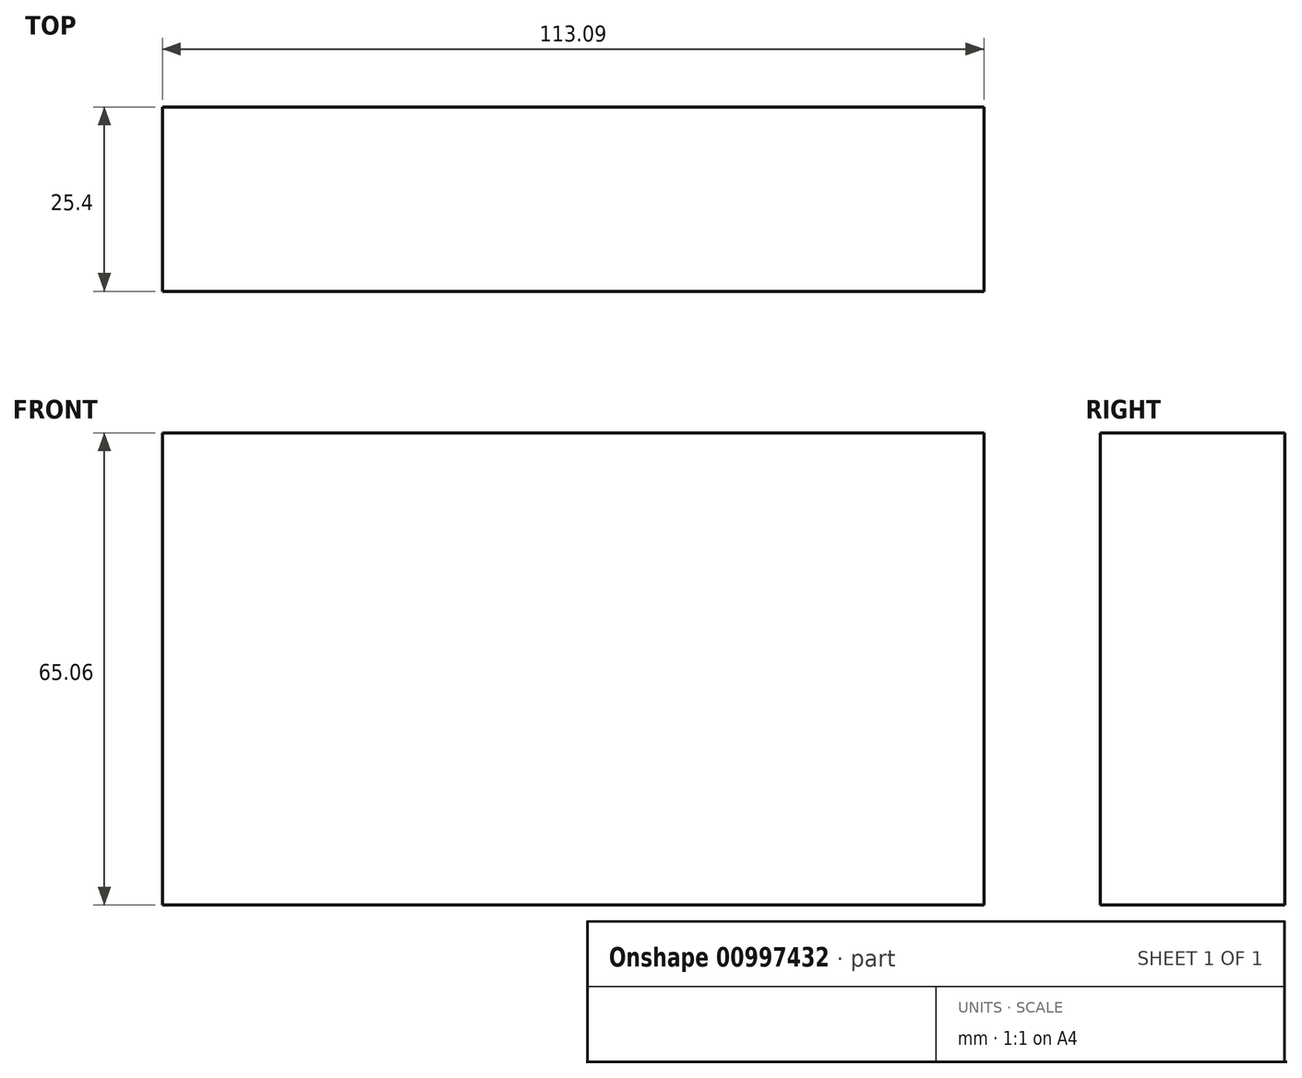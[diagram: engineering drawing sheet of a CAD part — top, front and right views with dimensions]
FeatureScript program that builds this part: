
annotation { "Feature Type Name" : "Feature", "Feature Type Description" : "" }
export const myFeature = defineFeature(function(context is Context, id is Id, definition is map)
    precondition{}
    {
        {
            var Q0;
            Q0=qCreatedBy(makeId("Front.planeOp"),FACE);
            var sketch = newSketch(context, id + "F0", { "sketchPlane" : qUnion([Q0])});
            skLineSegment(sketch, "E0.bottom", {"start": v(-66.89, 30.01) * mm, "end": v(46.2, 30.01) * mm});
            skLineSegment(sketch, "E0.top", {"start": v(-66.89, -35.05) * mm, "end": v(46.2, -35.05) * mm});
            skLineSegment(sketch, "E0.left", {"start": v(-66.89, 30.01) * mm, "end": v(-66.89, -35.05) * mm});
            skLineSegment(sketch, "E0.right", {"start": v(46.2, 30.01) * mm, "end": v(46.2, -35.05) * mm});
            skSolve(sketch);
        }
        {
            var Q0;
            Q0=makeQuery(id+"F0.imprint","IMPRINT",FACE,{"disambiguationData":[TD([[makeQuery(id+"F0.imprint","IMPRINT",EDGE,{"derivedFrom":sQuery(id+"F0.wireOp",EDGE,"E0.bottom")}),-1.0]])]});
            extrude(context, id + "F1", {"entities" : qUnion([Q0]), "depth" : 25.4 * mm, "offsetDistance" : 25.4 * mm});
        }
    });
